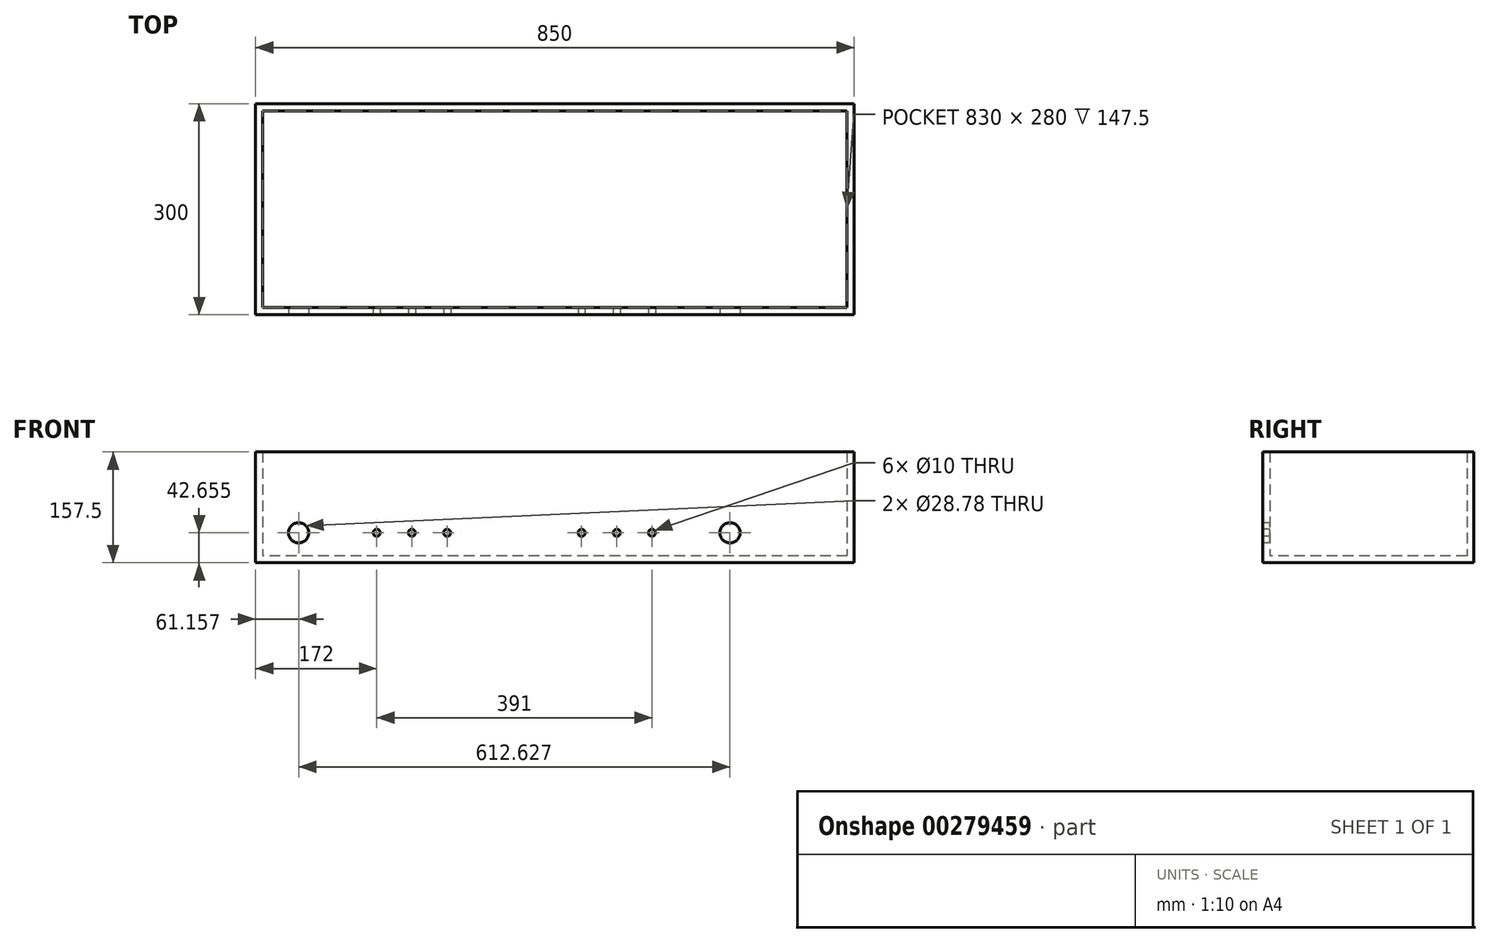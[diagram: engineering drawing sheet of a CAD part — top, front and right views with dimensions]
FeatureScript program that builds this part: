
annotation { "Feature Type Name" : "Feature", "Feature Type Description" : "" }
export const myFeature = defineFeature(function(context is Context, id is Id, definition is map)
    precondition{}
    {
        {
            var Q0;
            Q0=qCreatedBy(makeId("Top.planeOp"),FACE);
            var sketch = newSketch(context, id + "F0", { "sketchPlane" : qUnion([Q0])});
            skLineSegment(sketch, "E0.bottom", {"start": v(425, 150) * mm, "end": v(-425, 150) * mm});
            skLineSegment(sketch, "E0.top", {"start": v(425, -150) * mm, "end": v(-425, -150) * mm});
            skLineSegment(sketch, "E0.left", {"start": v(425, 150) * mm, "end": v(425, -150) * mm});
            skLineSegment(sketch, "E0.right", {"start": v(-425, 150) * mm, "end": v(-425, -150) * mm});
            skPoint(sketch, "E0.middle", {"position": v(0, 0) * mm});
            skSolve(sketch);
        }
        {
            var Q0;
            Q0=makeQuery(id+"F0.imprint","IMPRINT",FACE,{"disambiguationData":[TD([[makeQuery(id+"F0.imprint","IMPRINT",EDGE,{"derivedFrom":sQuery(id+"F0.wireOp",EDGE,"E0.bottom")}),1.0]])]});
            extrude(context, id + "F1", {"entities" : qUnion([Q0]), "depth" : 7.5 * mm});
        }
        {
            var Q0;
            Q0=makeQuery(id+"F1.opExtrude","CAP_FACE",FACE,{"disambiguationData":[OSD([sQuery(id+"F0.wireOp",EDGE,"E0.bottom"),sQuery(id+"F0.wireOp",EDGE,"E0.top"),sQuery(id+"F0.wireOp",EDGE,"E0.left"),sQuery(id+"F0.wireOp",EDGE,"E0.right")])],"isStart":false});
            var sketch = newSketch(context, id + "F2", { "sketchPlane" : qUnion([Q0])});
            skLineSegment(sketch, "E1.bottom", {"start": v(417.5, 142.5) * mm, "end": v(-417.5, 142.5) * mm});
            skLineSegment(sketch, "E1.top", {"start": v(417.5, -142.5) * mm, "end": v(-417.5, -142.5) * mm});
            skLineSegment(sketch, "E1.left", {"start": v(417.5, 142.5) * mm, "end": v(417.5, -142.5) * mm});
            skLineSegment(sketch, "E1.right", {"start": v(-417.5, 142.5) * mm, "end": v(-417.5, -142.5) * mm});
            skPoint(sketch, "E1.middle", {"position": v(0, 0) * mm});
            skLineSegment(sketch, "E2.bottom", {"start": v(425, 150) * mm, "end": v(-425, 150) * mm});
            skLineSegment(sketch, "E2.top", {"start": v(425, -150) * mm, "end": v(-425, -150) * mm});
            skLineSegment(sketch, "E2.left", {"start": v(425, 150) * mm, "end": v(425, -150) * mm});
            skLineSegment(sketch, "E2.right", {"start": v(-425, 150) * mm, "end": v(-425, -150) * mm});
            skSolve(sketch);
        }
        {
            var Q0;
            Q0 = qSketchRegion(id + "F2", true);
            extrude(context, id + "F3", {"entities" : qUnion([Q0]), "operationType" : NewBodyOperationType.ADD, "depth" : 150 * mm});
        }
        {
            var Q0;
            Q0=makeQuery(id+"F1.opExtrude","CAP_FACE",FACE,{"disambiguationData":[OSD([sQuery(id+"F0.wireOp",EDGE,"E0.bottom"),sQuery(id+"F0.wireOp",EDGE,"E0.top"),sQuery(id+"F0.wireOp",EDGE,"E0.left"),sQuery(id+"F0.wireOp",EDGE,"E0.right")])],"isStart":false});
            extrude(context, id + "F4", {"entities" : qUnion([Q0]), "depth" : 2.5 * mm});
        }
        {
            var Q0;
            Q0=makeQuery(id+"F4.opExtrude","CAP_FACE",FACE,{"disambiguationData":[OSD([sQuery(id+"F0.wireOp",EDGE,"E0.bottom"),sQuery(id+"F0.wireOp",EDGE,"E0.top"),sQuery(id+"F0.wireOp",EDGE,"E0.left"),sQuery(id+"F0.wireOp",EDGE,"E0.right")])],"isStart":false});
            var sketch = newSketch(context, id + "F5", { "sketchPlane" : qUnion([Q0])});
            skLineSegment(sketch, "E3.bottom", {"start": v(415, 140) * mm, "end": v(-415, 140) * mm});
            skLineSegment(sketch, "E3.top", {"start": v(415, -140) * mm, "end": v(-415, -140) * mm});
            skLineSegment(sketch, "E3.left", {"start": v(415, 140) * mm, "end": v(415, -140) * mm});
            skLineSegment(sketch, "E3.right", {"start": v(-415, 140) * mm, "end": v(-415, -140) * mm});
            skPoint(sketch, "E3.middle", {"position": v(0, 0) * mm});
            skLineSegment(sketch, "E4.bottom", {"start": v(417.5, 142.5) * mm, "end": v(-417.5, 142.5) * mm});
            skLineSegment(sketch, "E4.top", {"start": v(417.5, -142.5) * mm, "end": v(-417.5, -142.5) * mm});
            skLineSegment(sketch, "E4.left", {"start": v(417.5, 142.5) * mm, "end": v(417.5, -142.5) * mm});
            skLineSegment(sketch, "E4.right", {"start": v(-417.5, 142.5) * mm, "end": v(-417.5, -142.5) * mm});
            skSolve(sketch);
        }
        {
            var Q0;
            Q0 = qSketchRegion(id + "F5", true);
            extrude(context, id + "F6", {"entities" : qUnion([Q0]), "operationType" : NewBodyOperationType.ADD, "depth" : 147.5 * mm});
        }
        {
            var Q0;
            Q0=makeQuery(id+"F3.boolean.opBoolean","MERGE",FACE,{"derivedFrom":[makeQuery(id+"F1.opExtrude","SWEPT_FACE",FACE,{"disambiguationData":[OSD([sQuery(id+"F0.wireOp",EDGE,"E0.top")])]}),makeQuery(id+"F3.opExtrude","SWEPT_FACE",FACE,{"disambiguationData":[OSD([sQuery(id+"F2.wireOp",EDGE,"E2.top")])]})]});
            var sketch = newSketch(context, id + "F7", { "sketchPlane" : qUnion([Q0])});
            skLineSegment(sketch, "E5.bottom", {"start": v(280, 144.85) * mm, "end": v(-395, 144.84) * mm, "construction": true});
            skLineSegment(sketch, "E5.top", {"start": v(280, 12.66) * mm, "end": v(-395, 12.66) * mm, "construction": true});
            skLineSegment(sketch, "E5.left", {"start": v(280, 144.85) * mm, "end": v(280, 12.66) * mm, "construction": true});
            skLineSegment(sketch, "E5.right", {"start": v(-395, 144.84) * mm, "end": v(-395, 12.66) * mm, "construction": true});
            skPoint(sketch, "E5.middle", {"position": v(0, 78.75) * mm});
            skPoint(sketch, "E5.middle.positionSnap0", {"position": v(-425, 78.75) * mm});
            skPoint(sketch, "E5.centerSnap0", {"position": v(-425, 78.75) * mm});
            skCircle(sketch, "E6", {"center": v(-153, 42.66) * mm, "radius": 5 * mm});
            skCircle(sketch, "E7", {"center": v(38, 42.66) * mm, "radius": 5 * mm});
            skLineSegment(sketch, "E8", {"start": v(-153, 42.66) * mm, "end": v(-153, 12.66) * mm, "construction": true});
            skLineSegment(sketch, "E9", {"start": v(-153, 42.66) * mm, "end": v(-395, 42.65) * mm, "construction": true});
            skLineSegment(sketch, "E10", {"start": v(38, 42.66) * mm, "end": v(38, 12.66) * mm, "construction": true});
            skLineSegment(sketch, "E11", {"start": v(38, 42.66) * mm, "end": v(280, 42.66) * mm, "construction": true});
            skCircle(sketch, "E12.1.0.0", {"center": v(88, 42.66) * mm, "radius": 5 * mm});
            skCircle(sketch, "E12.2.0.0", {"center": v(138, 42.66) * mm, "radius": 5 * mm});
            skLineSegment(sketch, "E12.direction1", {"start": v(38, 42.66) * mm, "end": v(88, 42.66) * mm, "construction": true});
            skCircle(sketch, "E13.1.0.0", {"center": v(-203, 42.66) * mm, "radius": 5 * mm});
            skCircle(sketch, "E13.2.0.0", {"center": v(-253, 42.66) * mm, "radius": 5 * mm});
            skLineSegment(sketch, "E13.direction1", {"start": v(-153, 42.66) * mm, "end": v(-203, 42.66) * mm, "construction": true});
            skCircle(sketch, "E14", {"center": v(248.78, 42.66) * mm, "radius": 14.4 * mm});
            skCircle(sketch, "E15.1.0.0", {"center": v(-363.84, 42.66) * mm, "radius": 14.4 * mm});
            skLineSegment(sketch, "E15.direction1", {"start": v(248.78, 42.66) * mm, "end": v(-363.84, 42.66) * mm, "construction": true});
            skSolve(sketch);
        }
        {
            var Q0;
            Q0 = qSketchRegion(id + "F7", true);
            extrude(context, id + "F8", {"entities" : qUnion([Q0]), "operationType" : NewBodyOperationType.REMOVE, "oppositeDirection" : true, "depth" : 25 * mm});
        }
    });
